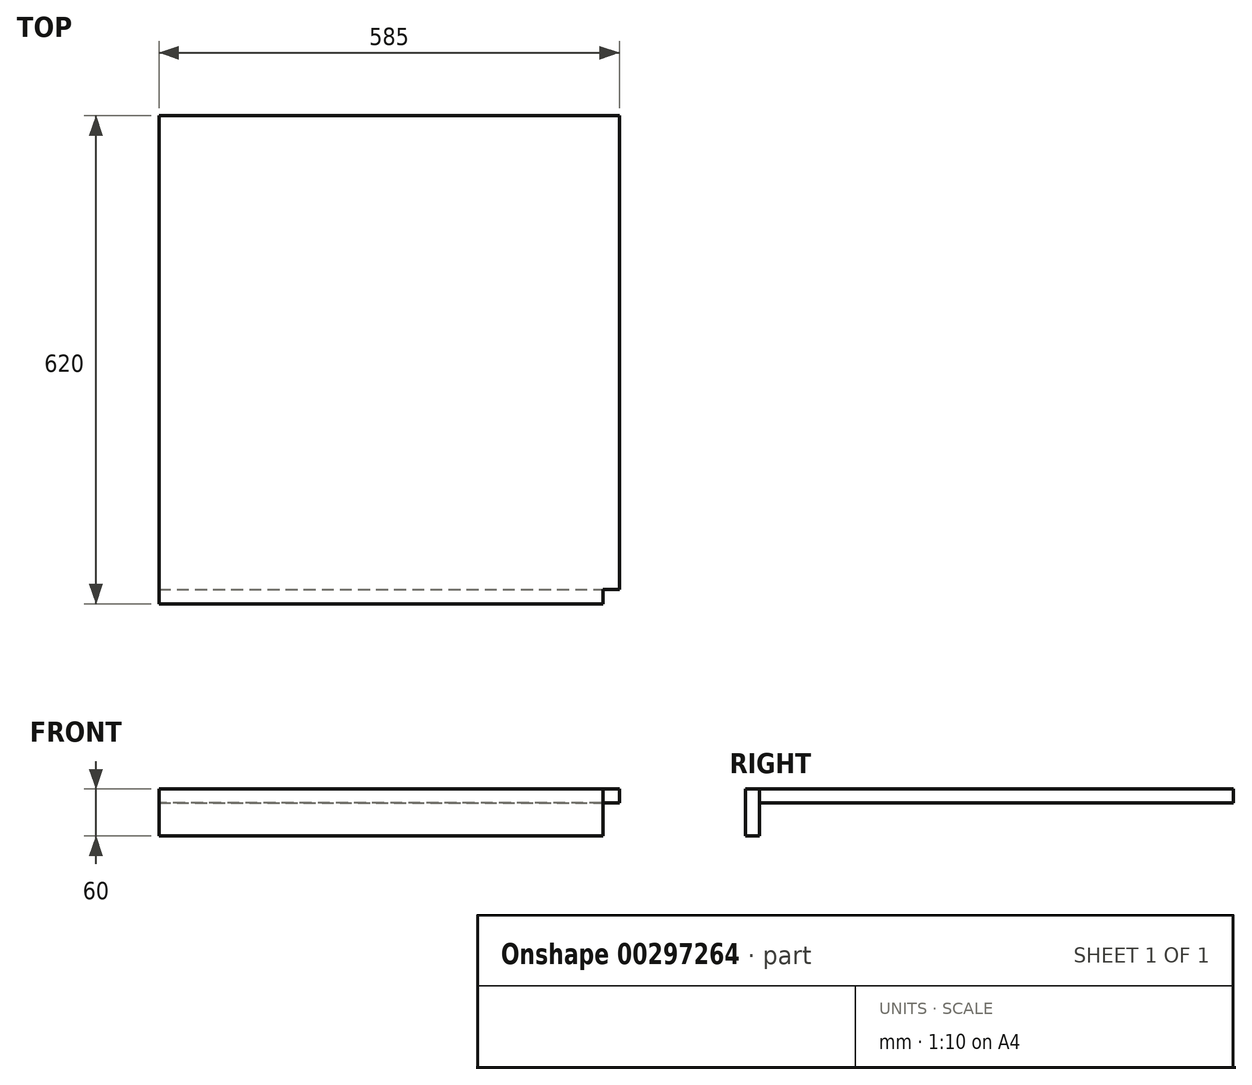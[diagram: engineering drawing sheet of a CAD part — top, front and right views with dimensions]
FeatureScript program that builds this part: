
annotation { "Feature Type Name" : "Feature", "Feature Type Description" : "" }
export const myFeature = defineFeature(function(context is Context, id is Id, definition is map)
    precondition{}
    {
        {
            var Q0;
            Q0=qCreatedBy(makeId("Top.planeOp"),FACE);
            var sketch = newSketch(context, id + "F0", { "sketchPlane" : qUnion([Q0])});
            skLineSegment(sketch, "E0.bottom", {"start": v(292.5, -310) * mm, "end": v(-292.5, -310) * mm});
            skLineSegment(sketch, "E0.top", {"start": v(292.5, 310) * mm, "end": v(-292.5, 310) * mm});
            skLineSegment(sketch, "E0.left", {"start": v(292.5, -310) * mm, "end": v(292.5, 310) * mm});
            skLineSegment(sketch, "E0.right", {"start": v(-292.5, -310) * mm, "end": v(-292.5, 310) * mm});
            skPoint(sketch, "E0.middle", {"position": v(0, 0) * mm});
            skSolve(sketch);
        }
        {
            var Q0;
            Q0 = qSketchRegion(id + "F0", true);
            extrude(context, id + "F1", {"entities" : qUnion([Q0]), "depth" : 18 * mm});
        }
        {
            var Q0;
            Q0=makeQuery(id+"F1.opExtrude","CAP_FACE",FACE,{"disambiguationData":[OSD([sQuery(id+"F0.wireOp",EDGE,"E0.bottom"),sQuery(id+"F0.wireOp",EDGE,"E0.top"),sQuery(id+"F0.wireOp",EDGE,"E0.left"),sQuery(id+"F0.wireOp",EDGE,"E0.right")])],"isStart":true});
            var sketch = newSketch(context, id + "F2", { "sketchPlane" : qUnion([Q0])});
            skLineSegment(sketch, "E1.bottom", {"start": v(-292.5, 310) * mm, "end": v(292.5, 310) * mm});
            skLineSegment(sketch, "E1.top", {"start": v(-292.5, 292) * mm, "end": v(292.5, 292) * mm});
            skLineSegment(sketch, "E1.left", {"start": v(-292.5, 310) * mm, "end": v(-292.5, 292) * mm});
            skLineSegment(sketch, "E1.right", {"start": v(292.5, 310) * mm, "end": v(292.5, 292) * mm});
            skSolve(sketch);
        }
        {
            var Q0;
            Q0 = qSketchRegion(id + "F2", true);
            extrude(context, id + "F3", {"entities" : qUnion([Q0]), "operationType" : NewBodyOperationType.ADD, "depth" : 42 * mm});
        }
        {
            var Q0;
            Q0=makeQuery(id+"F1.opExtrude","CAP_FACE",FACE,{"disambiguationData":[OSD([sQuery(id+"F0.wireOp",EDGE,"E0.bottom"),sQuery(id+"F0.wireOp",EDGE,"E0.top"),sQuery(id+"F0.wireOp",EDGE,"E0.left"),sQuery(id+"F0.wireOp",EDGE,"E0.right")])],"isStart":false});
            var sketch = newSketch(context, id + "F4", { "sketchPlane" : qUnion([Q0])});
            skLineSegment(sketch, "E2.bottom", {"start": v(292.5, -310) * mm, "end": v(271.5, -310) * mm});
            skLineSegment(sketch, "E2.top", {"start": v(292.5, -292) * mm, "end": v(271.5, -292) * mm});
            skLineSegment(sketch, "E2.left", {"start": v(292.5, -310) * mm, "end": v(292.5, -292) * mm});
            skLineSegment(sketch, "E2.right", {"start": v(271.5, -310) * mm, "end": v(271.5, -292) * mm});
            skSolve(sketch);
        }
        {
            var Q0;
            Q0 = qSketchRegion(id + "F4", true);
            extrude(context, id + "F5", {"entities" : qUnion([Q0]), "operationType" : NewBodyOperationType.REMOVE, "oppositeDirection" : true, "depth" : 60 * mm});
        }
    });
